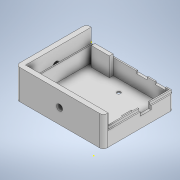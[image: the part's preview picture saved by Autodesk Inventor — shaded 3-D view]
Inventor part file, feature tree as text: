
AUTODESK INVENTOR PART (.ipt)
format: ipt  version: 2022 (Build 260153000, 153)  size: 301,056 bytes
history: native  units: in
note: dims shown in document units (in); Inventor stores cm internally (conversion verified against a paired STEP export)
features: extrude x12, sketch x10, fillet x4
ambient origin geometry x8: Origin, YZ Plane, XZ Plane, XY Plane, X Axis, Y Axis, Z Axis, Center Point
bodies: Solid1 (feature_tree)
feature tree (26):
  sketch  "Sketch1"  dims[d0=2.6772in d2=0.5512in d3=0.0in]
  extrude  "Extrusion1"  Depth=0.5512in TaperAngle=0.0deg
  sketch  "Sketch3"  dims[d5=0.0787in d6=0.0787in]
  extrude  "Extrusion2"  Depth=0.0787in
  extrude  "Extrusion3"  Depth=0.0787in
  extrude  "Extrusion4"  Depth=0.0787in TaperAngle=0.0deg
  extrude  "Extrusion5"  Depth=0.0787in TaperAngle=0.0deg
  extrude  "Extrusion6"  Depth=0.1181in
  extrude  "Extrusion7"  Depth=0.6102in TaperAngle=0.0deg
  extrude  "Extrusion9"  Depth=0.0787in
  fillet  "Fillet7"  Radius=0.0394in
  fillet  "Fillet9"  Radius=0.1181in
  extrude  "Extrusion11"  Depth=0.9646in TaperAngle=0.0deg
  extrude  "Extrusion12"  Depth=0.0197in
  extrude  "Extrusion13"  Depth=0.315in
  extrude  "Extrusion14"  Depth=0.1181in
  fillet  "Fillet12"  Radius=0.3543in
  fillet  "Fillet13"  Radius=1.0933in
  sketch  "Sketch4"  dims[d7=0.0787in d11=0.0787in]
  sketch  "Sketch7"  dims[d13=0.5118in d14=0.0in d44=0.0787in d45=0.0in]
  sketch  "Sketch10"  dims[d46=2.6772in d48=0.0787in d49=0.0in]
  sketch  "Sketch11"  dims[d57=0.5906in d58=0.1181in]
  sketch  "Sketch17"  dims[d61=0.5906in d64=0.6102in d65=0.0in]
  sketch  "Sketch18"  dims[d72=0.3543in d73=0.0in d75=0.0787in d76=0.0394in d79=0.1181in]
  sketch  "Sketch19"  dims[d81=0.1575in d82=0.9646in d83=0.0in]
  sketch  "Sketch20"  dims[d85=0.9161in d86=0.8465in d88=0.315in d89=0.1181in d108=0.3543in d109=0.1969in d111=1.0933in d114=0.3937in d115=0.0in d119=0.4528in d120=0.3937in d121=0.1181in d123=0.1181in d132=1.9685in d133=2.5197in d138=2.126in d139=0.0394in d140=0.0394in d141=0.0394in d144=0.0in d151=0.3346in d152=0.3346in d153=0.1969in d157=0.0in d158=0.5315in d160=1.126in d161=0.3937in d162=0.0in d169=0.1575in d170=0.315in d171=0.315in d172=0.0394in d173=0.0in d174=0.0in d177=1.4173in d178=0.1969in d179=0.1575in d180=0.0in d181=0.1969in d182=0.1575in d183=0.0in d184=0.1181in d185=0.1181in d40=0.0197in d41=0.0344in d42=0.0197in d43=0.0344in d66=0.0197in d67=0.0344in d84=0.0197in d186=0.0197in d187=0.0344in d188=0.0197in d189=0.0344in]
